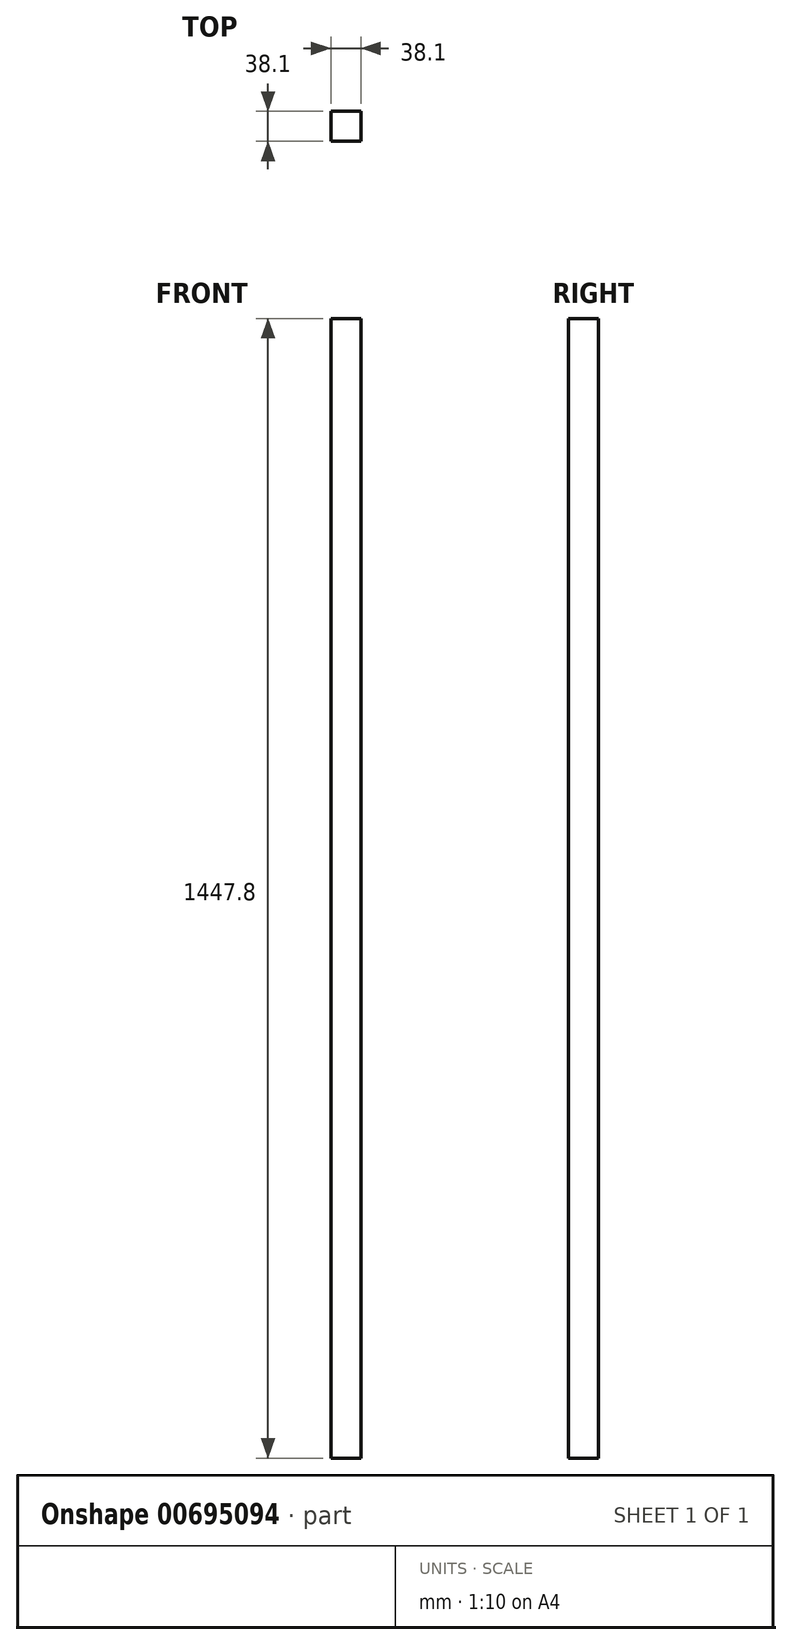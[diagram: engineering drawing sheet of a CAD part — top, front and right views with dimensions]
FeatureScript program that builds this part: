
annotation { "Feature Type Name" : "Feature", "Feature Type Description" : "" }
export const myFeature = defineFeature(function(context is Context, id is Id, definition is map)
    precondition{}
    {
        {
            var Q0;
            Q0=qCreatedBy(makeId("Top.planeOp"),FACE);
            var sketch = newSketch(context, id + "F0", { "sketchPlane" : qUnion([Q0])});
            skLineSegment(sketch, "E0.bottom", {"start": v(0, 0) * mm, "end": v(38.1, 0) * mm});
            skLineSegment(sketch, "E0.top", {"start": v(0, 38.1) * mm, "end": v(38.1, 38.1) * mm});
            skLineSegment(sketch, "E0.left", {"start": v(0, 0) * mm, "end": v(0, 38.1) * mm});
            skLineSegment(sketch, "E0.right", {"start": v(38.1, 0) * mm, "end": v(38.1, 38.1) * mm});
            skSolve(sketch);
        }
        {
            var Q0;
            Q0=makeQuery(id+"F0.imprint","IMPRINT",FACE,{"disambiguationData":[TD([[makeQuery(id+"F0.imprint","IMPRINT",EDGE,{"derivedFrom":sQuery(id+"F0.wireOp",EDGE,"E0.bottom")}),1.0]])]});
            extrude(context, id + "F1", {"entities" : qUnion([Q0]), "depth" : 1447.8 * mm, "offsetDistance" : 25.4 * mm});
        }
    });
